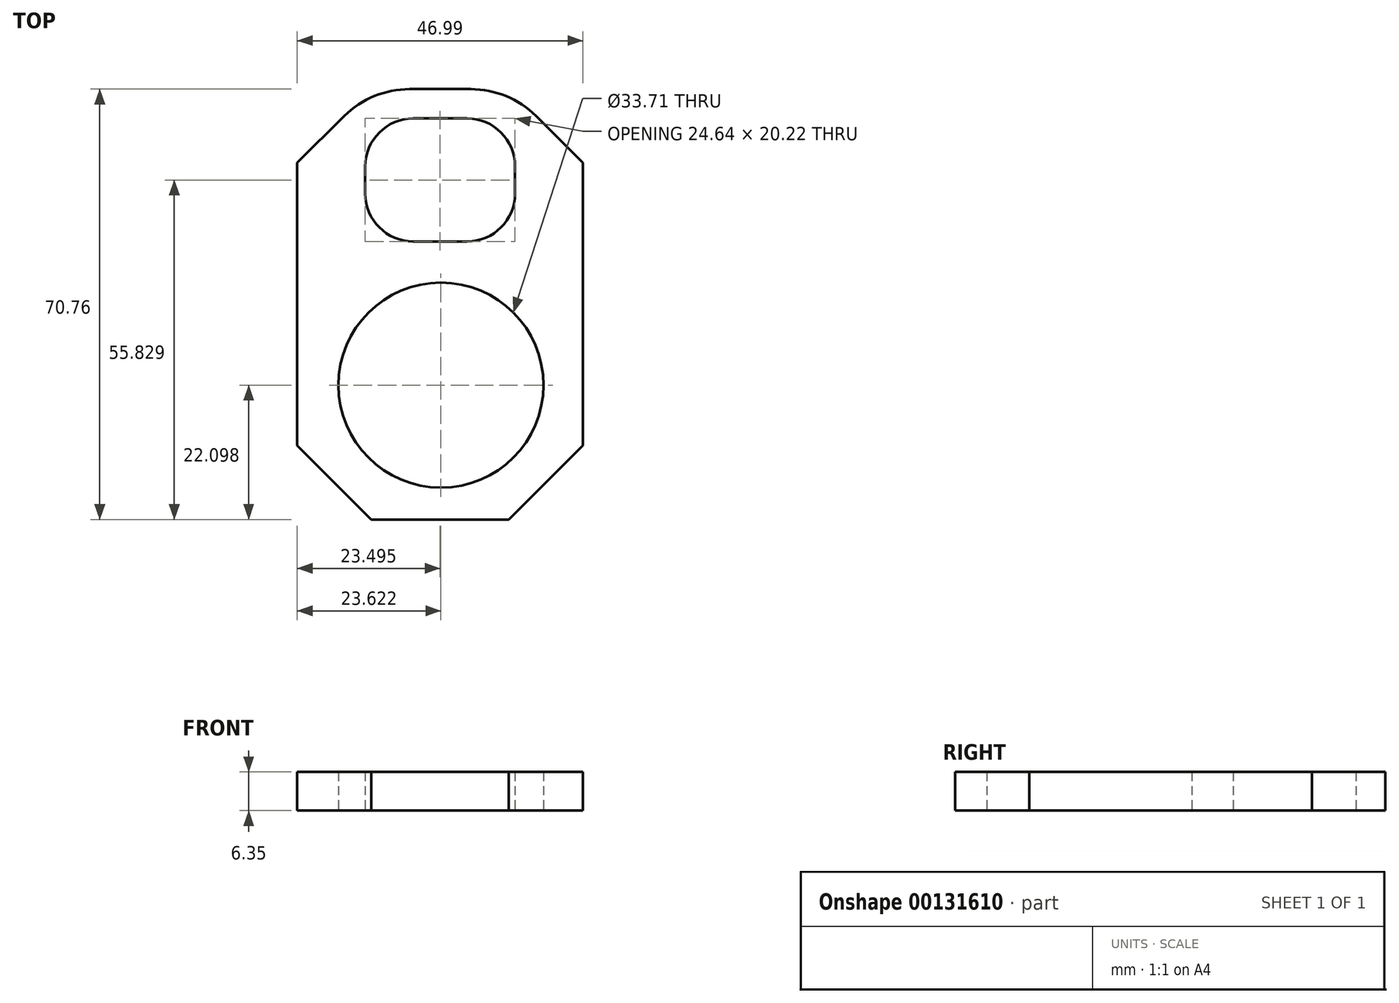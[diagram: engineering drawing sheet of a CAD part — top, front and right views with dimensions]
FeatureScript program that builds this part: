
annotation { "Feature Type Name" : "Feature", "Feature Type Description" : "" }
export const myFeature = defineFeature(function(context is Context, id is Id, definition is map)
    precondition{}
    {
        {
            var Q0;
            Q0=qCreatedBy(makeId("Top.planeOp"),FACE);
            var sketch = newSketch(context, id + "F0", { "sketchPlane" : qUnion([Q0])});
            skLineSegment(sketch, "E0.bottom", {"start": v(12.2, 0) * mm, "end": v(34.8, 0) * mm});
            skLineSegment(sketch, "E0.top", {"start": v(18.47, 70.76) * mm, "end": v(28.52, 70.76) * mm});
            skCircle(sketch, "E1", {"center": v(23.62, 22.1) * mm, "radius": 16.85 * mm});
            skPoint(sketch, "E2", {"position": v(12.2, 0) * mm});
            skPoint(sketch, "E3", {"position": v(0, 12.2) * mm});
            skLineSegment(sketch, "E4", {"start": v(0, 12.2) * mm, "end": v(12.2, 0) * mm});
            skPoint(sketch, "E5.orphan", {"position": v(0, 0) * mm});
            skLineSegment(sketch, "E6.MirrorCS", {"start": v(46.99, 12.2) * mm, "end": v(34.8, 0) * mm});
            skPoint(sketch, "E7.MirrorP", {"position": v(46.99, 12.2) * mm});
            skPoint(sketch, "E8.MirrorP", {"position": v(34.8, 0) * mm});
            skPoint(sketch, "E9.orphan", {"position": v(47, 0) * mm});
            skLineSegment(sketch, "E10.bottom", {"start": v(19.05, 65.94) * mm, "end": v(27.94, 65.94) * mm});
            skLineSegment(sketch, "E10.top", {"start": v(19.05, 45.72) * mm, "end": v(27.94, 45.72) * mm});
            skLineSegment(sketch, "E10.left", {"start": v(11.18, 58.06) * mm, "end": v(11.18, 53.6) * mm});
            skLineSegment(sketch, "E10.right", {"start": v(35.81, 58.06) * mm, "end": v(35.81, 53.6) * mm});
            skPoint(sketch, "E11.visualSharp", {"position": v(11.18, 65.94) * mm});
            skArc(sketch, "E11.filletArc", {"start": v(19.05, 65.94) * mm, "mid": v(13.48, 63.63) * mm, "end": v(11.18, 58.06) * mm});
            skPoint(sketch, "E12.visualSharp", {"position": v(35.81, 65.94) * mm});
            skArc(sketch, "E12.filletArc", {"start": v(35.81, 58.06) * mm, "mid": v(33.5, 63.63) * mm, "end": v(27.94, 65.94) * mm});
            skPoint(sketch, "E13.visualSharp", {"position": v(35.81, 45.72) * mm});
            skArc(sketch, "E13.filletArc", {"start": v(27.94, 45.72) * mm, "mid": v(33.5, 48.03) * mm, "end": v(35.81, 53.6) * mm});
            skPoint(sketch, "E14.visualSharp", {"position": v(11.18, 45.72) * mm});
            skArc(sketch, "E14.filletArc", {"start": v(11.18, 53.6) * mm, "mid": v(13.48, 48.03) * mm, "end": v(19.05, 45.72) * mm});
            skPoint(sketch, "E15", {"position": v(12.2, 70.76) * mm});
            skPoint(sketch, "E16.MirrorP", {"position": v(34.8, 70.76) * mm});
            skPoint(sketch, "E17", {"position": v(0, 58.67) * mm});
            skPoint(sketch, "E18.MirrorP", {"position": v(46.99, 58.67) * mm});
            skLineSegment(sketch, "E19", {"start": v(0, 58.67) * mm, "end": v(7.74, 66.35) * mm});
            skLineSegment(sketch, "E20", {"start": v(39.25, 66.35) * mm, "end": v(46.99, 58.67) * mm});
            skPoint(sketch, "E21.orphan", {"position": v(0, 70.76) * mm});
            skPoint(sketch, "E22.orphan", {"position": v(46.99, 70.76) * mm});
            skArc(sketch, "E23.filletArc", {"start": v(18.47, 70.76) * mm, "mid": v(12.66, 69.62) * mm, "end": v(7.74, 66.35) * mm});
            skArc(sketch, "E24.filletArc", {"start": v(39.25, 66.35) * mm, "mid": v(34.33, 69.62) * mm, "end": v(28.52, 70.76) * mm});
            skPoint(sketch, "E25.orphan", {"position": v(23.5, 70.76) * mm});
            skPoint(sketch, "E26.trimOffspring.end.orphan", {"position": v(23.5, 0) * mm});
            skLineSegment(sketch, "E27", {"start": v(0, 58.67) * mm, "end": v(0, 12.2) * mm});
            skLineSegment(sketch, "E28", {"start": v(46.99, 12.2) * mm, "end": v(46.99, 58.67) * mm});
            skSolve(sketch);
        }
        {
            var Q0;
            Q0=makeQuery(id+"F0.imprint","IMPRINT",FACE,{"disambiguationData":[TD([[makeQuery(id+"F0.imprint","IMPRINT",EDGE,{"derivedFrom":sQuery(id+"F0.wireOp",EDGE,"E0.bottom")}),1.0]])]});
            extrude(context, id + "F1", {"entities" : qUnion([Q0]), "depth" : 6.35 * mm});
        }
    });
